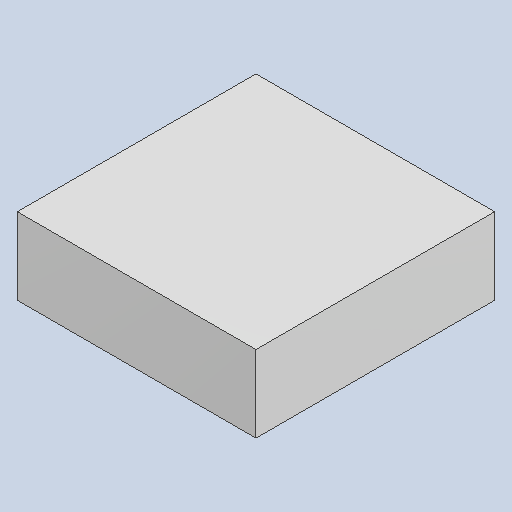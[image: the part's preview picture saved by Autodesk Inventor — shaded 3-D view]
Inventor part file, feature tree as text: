
AUTODESK INVENTOR PART (.ipt)
format: ipt  version: 2023.4 (Build 274418000, 418)  size: 79,872 bytes
history: native  units: mm
features: extrude x1
ambient origin geometry x8: Origin, YZ Plane, XZ Plane, XY Plane, X Axis, Y Axis, Z Axis, Center Point
bodies: Solid1 (feature_tree)
feature tree (1):
  extrude  "Extruded_4"  [1 undecoded]
note: 1 required parameter value undecoded (feature->parameter linkage not recoverable at this tier; creation-order binding heuristic only, values carry confidence <= 0.55)
